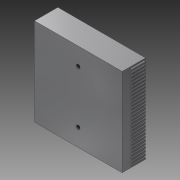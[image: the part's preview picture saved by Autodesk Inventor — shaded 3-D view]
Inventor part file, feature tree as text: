
AUTODESK INVENTOR PART (.ipt)
format: ipt  version: 2018.3 (Build 223284000, 284)  size: 265,728 bytes
history: native  units: mm
features: sketch x3, extrude x2, projected_geometry x2, direct_edit x1, hole x1, move_body x1
ambient origin geometry x8: Origin, YZ Plane, XZ Plane, XY Plane, X Axis, Y Axis, Z Axis, Center Point
bodies: Solid1 (feature_tree)
feature tree (10):
  extrude  "Extrusion1"  Depth=60.0mm
  extrude  "Extrusion2"  Depth=1.0mm
  direct_edit  "Direct Edit1"
  hole  "Hole1"  [1 undecoded]
  sketch  "Sketch1"  dims[d0=60.0mm d1=60.0mm]
  sketch  "Sketch2"  dims[d2=6.0mm d3=0.0mm d4=1.0mm]
  projected_geometry  "Projected Loop1"
  sketch  "Sketch3"  dims[d5=320.0mm d7=2.107mm d8=10.0mm d10=10.0mm d12=10.0mm d13=0.0mm d14=0.0mm d15=0.0mm d16=0.004mm d17=36.0mm d18=2.459mm d19=6.0mm d20=4.0mm d21=2.0mm d22=90.0deg d23=6.0mm d24=20.594885mm]
  projected_geometry  "Projected Loop2"
  move_body  "Move1"
note: 1 required parameter value undecoded (feature->parameter linkage not recoverable at this tier; creation-order binding heuristic only, values carry confidence <= 0.55)
